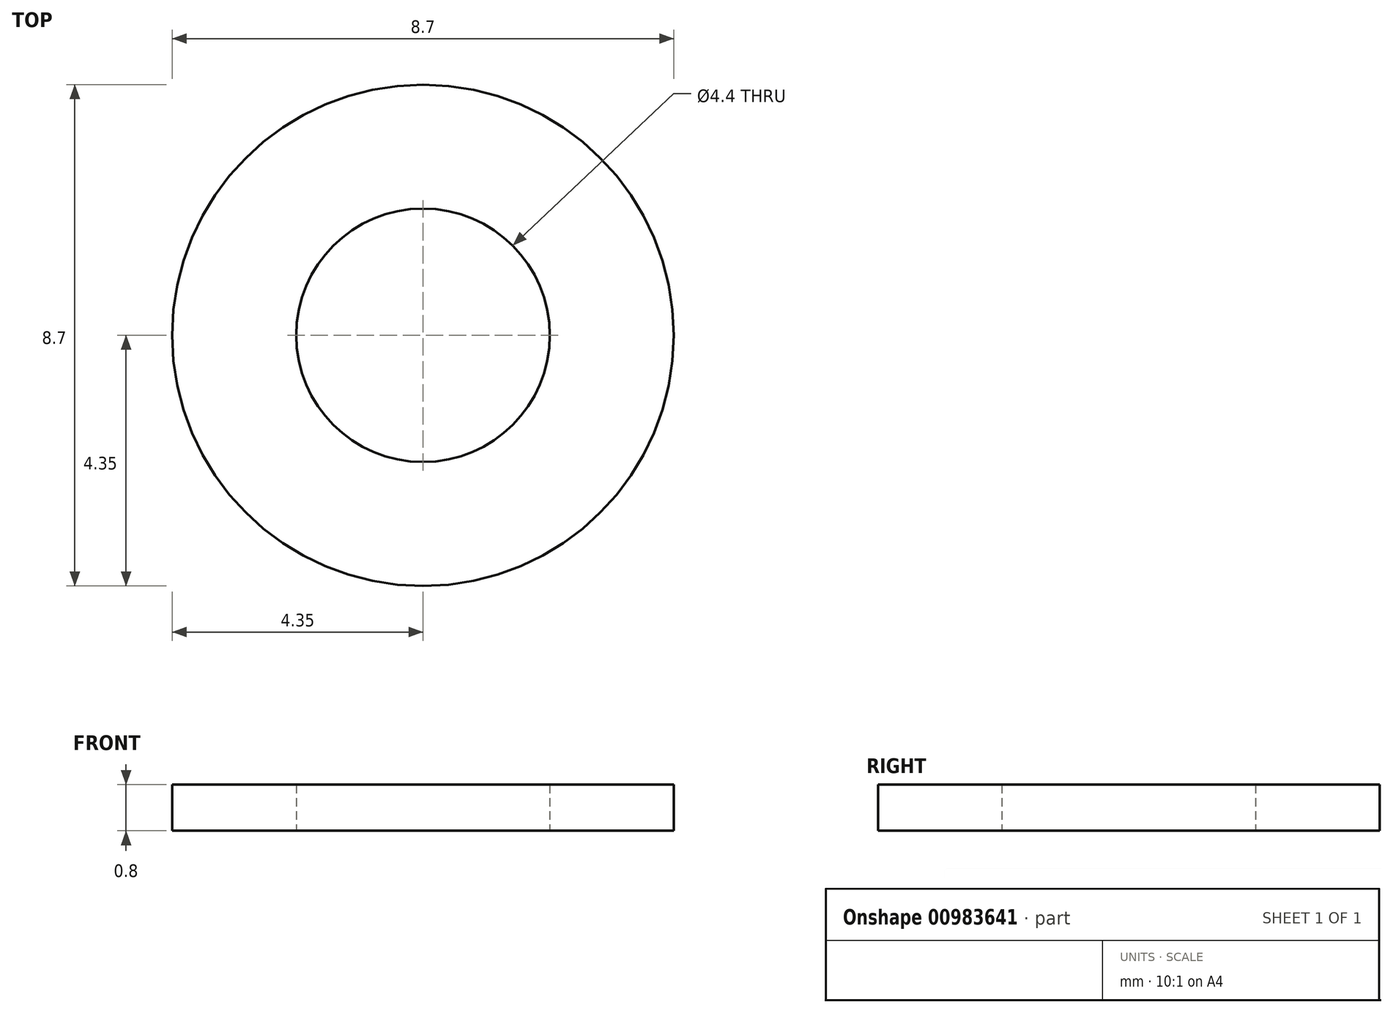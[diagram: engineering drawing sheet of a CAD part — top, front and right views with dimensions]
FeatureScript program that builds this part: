
annotation { "Feature Type Name" : "Feature", "Feature Type Description" : "" }
export const myFeature = defineFeature(function(context is Context, id is Id, definition is map)
    precondition{}
    {
        {
            assignVariable(context, id + "F0", {"name" : "RingH", "anyValue" : 0.8});
        }
        {
            var Q0;
            Q0=qCreatedBy(makeId("Top.planeOp"),FACE);
            var sketch = newSketch(context, id + "F1", { "sketchPlane" : qUnion([Q0])});
            skCircle(sketch, "E0", {"center": v(0, 0) * mm, "radius": 4.35 * mm});
            skCircle(sketch, "E1", {"center": v(0, 0) * mm, "radius": 2.2 * mm});
            skSolve(sketch);
        }
        {
            var Q0;
            Q0=makeQuery(id+"F1.imprint","IMPRINT",FACE,{"disambiguationData":[TD([[makeQuery(id+"F1.imprint","IMPRINT",EDGE,{"derivedFrom":sQuery(id+"F1.wireOp",EDGE,"E0")}),1.0]])]});
            extrude(context, id + "F2", {"entities" : qUnion([Q0]), "depth" : (getVariable(context, 'RingH')) * mm, "offsetDistance" : 25 * mm});
        }
    });
